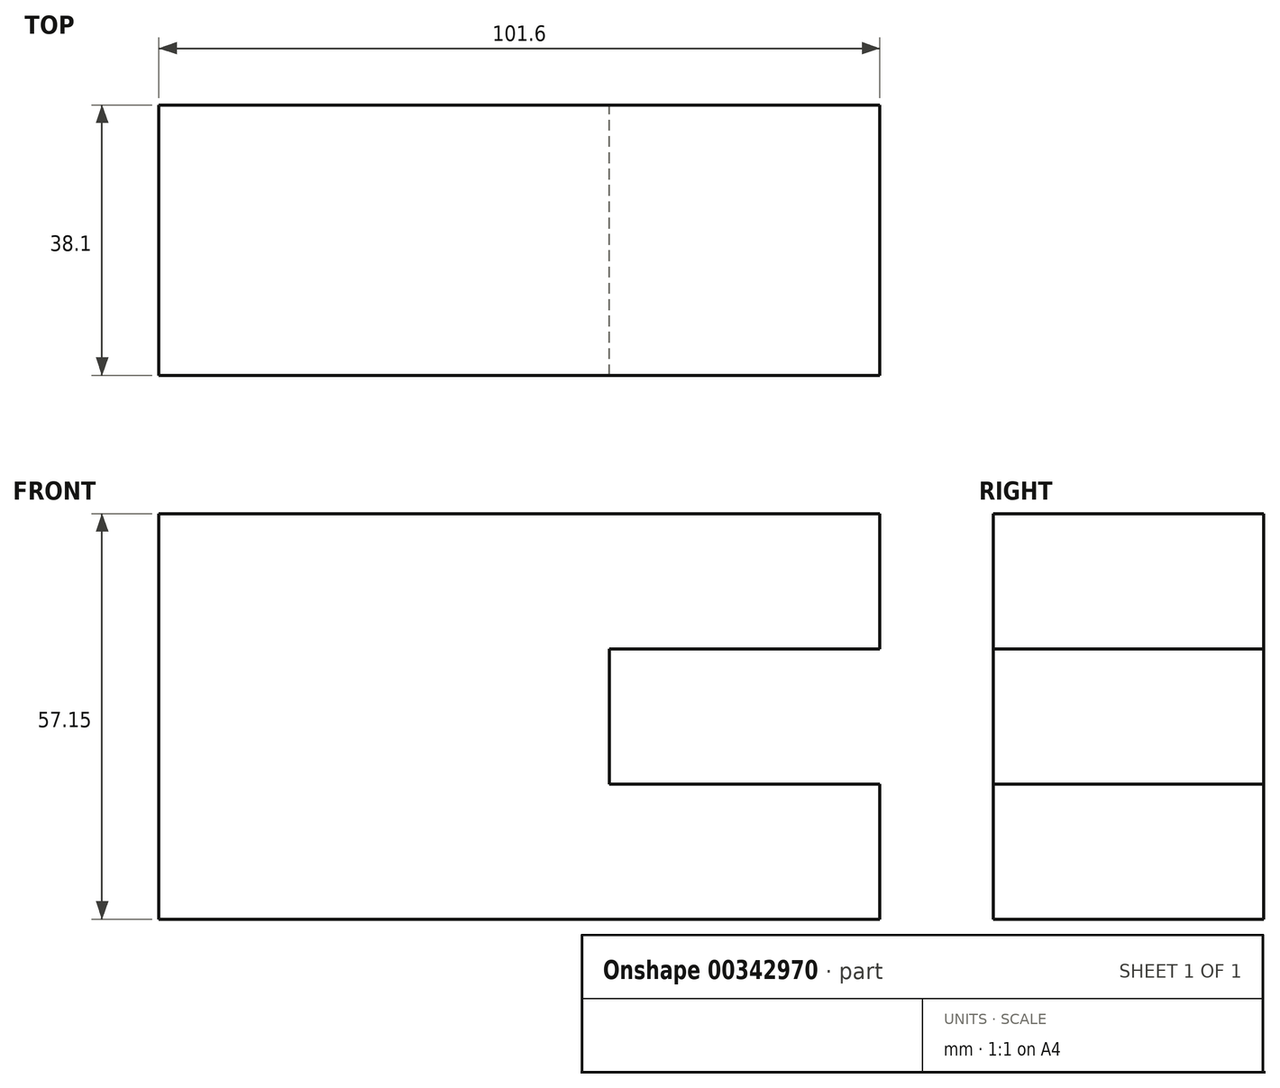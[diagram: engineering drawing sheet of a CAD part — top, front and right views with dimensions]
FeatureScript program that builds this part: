
annotation { "Feature Type Name" : "Feature", "Feature Type Description" : "" }
export const myFeature = defineFeature(function(context is Context, id is Id, definition is map)
    precondition{}
    {
        {
            var Q0;
            Q0=qCreatedBy(makeId("Front.planeOp"),FACE);
            var sketch = newSketch(context, id + "F0", { "sketchPlane" : qUnion([Q0])});
            skLineSegment(sketch, "E0", {"start": v(-52.17, 26.96) * mm, "end": v(49.43, 26.96) * mm});
            skLineSegment(sketch, "E1", {"start": v(49.43, 26.96) * mm, "end": v(49.43, 7.91) * mm});
            skLineSegment(sketch, "E2", {"start": v(49.43, 7.91) * mm, "end": v(11.33, 7.91) * mm});
            skLineSegment(sketch, "E3", {"start": v(11.33, 7.91) * mm, "end": v(11.33, -11.14) * mm});
            skLineSegment(sketch, "E4", {"start": v(11.33, -11.14) * mm, "end": v(49.43, -11.14) * mm});
            skLineSegment(sketch, "E5", {"start": v(49.43, -11.14) * mm, "end": v(49.43, -30.19) * mm});
            skLineSegment(sketch, "E6", {"start": v(49.43, -30.19) * mm, "end": v(-52.17, -30.19) * mm});
            skLineSegment(sketch, "E7", {"start": v(-52.17, -30.19) * mm, "end": v(-52.17, 26.96) * mm});
            skSolve(sketch);
        }
        {
            var Q0;
            Q0 = qSketchRegion(id + "F0", true);
            extrude(context, id + "F1", {"entities" : qUnion([Q0]), "depth" : 38.1 * mm});
        }
    });
